# Revit family: Kugelhahn mit Hebelgriff 2100
name_source: partatom
category: Rohrzubehör
units: mm (PartAtom-declared; Revit-internal decimal feet)

## family parameters
Arbeitsebenenbasiert = Nein
Beim Laden mit Abzugskörper schneiden = Nein
Bemaßung runder Anschluss = Durchmesser verwenden
Gemeinsam genutzt = Nein
Immer vertikal = Ja
OmniClass-Nummer = 23.65.55.14
OmniClass-Titel = Valves for Liquid Services
Teiletyp = Unterbricht

## types (1)
- Kugelhahn mit Hebelgriff 2100
    Anwendungen = Verwendung in Trinkwasseranlagen, überall dort wo eine lange Lebensdauer bei schwierigen Bedingungen gefordert ist.
    Gehäuse = entzinkungsbeständiges Pressmessing gemäß EN 12420 (Korrosionsbeständig)
    Griff = Aluminium, grün getaucht
    Hersteller = HERZ Armaturen Ges.m.b.H
    Hinweis = Gemäß Art 33 der REACH-Verordnung (EG Nr. 1907/2006) sind wir verpflichtet, darauf hinzuweisen, dass der Stoff Blei auf der SVHC-Liste geführt wird und dass alle aus Messing bestehenden Bauteile, die in unseren Erzeugnissen verarbeitet sind, mehr als 0,1 % (w/w) Blei (CAS: 7439-92-1 / EINECS: 231-100-4) enthalten.
Da Blei als Legierungsbestandteil fest gebunden ist, sind keine Expositionen zu erwarten und daher sind keine zusätzlichen Angaben zur sicheren Verwendung notwendig.
    Innengewinde = gemäß ISO 228
    Kugel = Pressmessing, Vollbohrung, verchromte Kugel mit glattem Durchgang
    Kugeldichtung = PTFE
    Max. Betriebsdruck = 2500000.0 Pa
    Max. Betriebstemperatur = 85 °C
    Medium = Trinkwasser
    SCTWCODE = 04;04:02
    SCTWSEQ = FW;SBT_TYP_FW="103";2
    Spindeldichtung = EPDM 70 ShA
    URL = www.herz-armaturen.at
    Vorgabe-Ansicht = 0 mm  [stored 0 ft]
    W01 = 135.00°

note: [stored X ft] marks values corroborated as IEEE doubles in the binary element streams (Revit-internal decimal feet)
